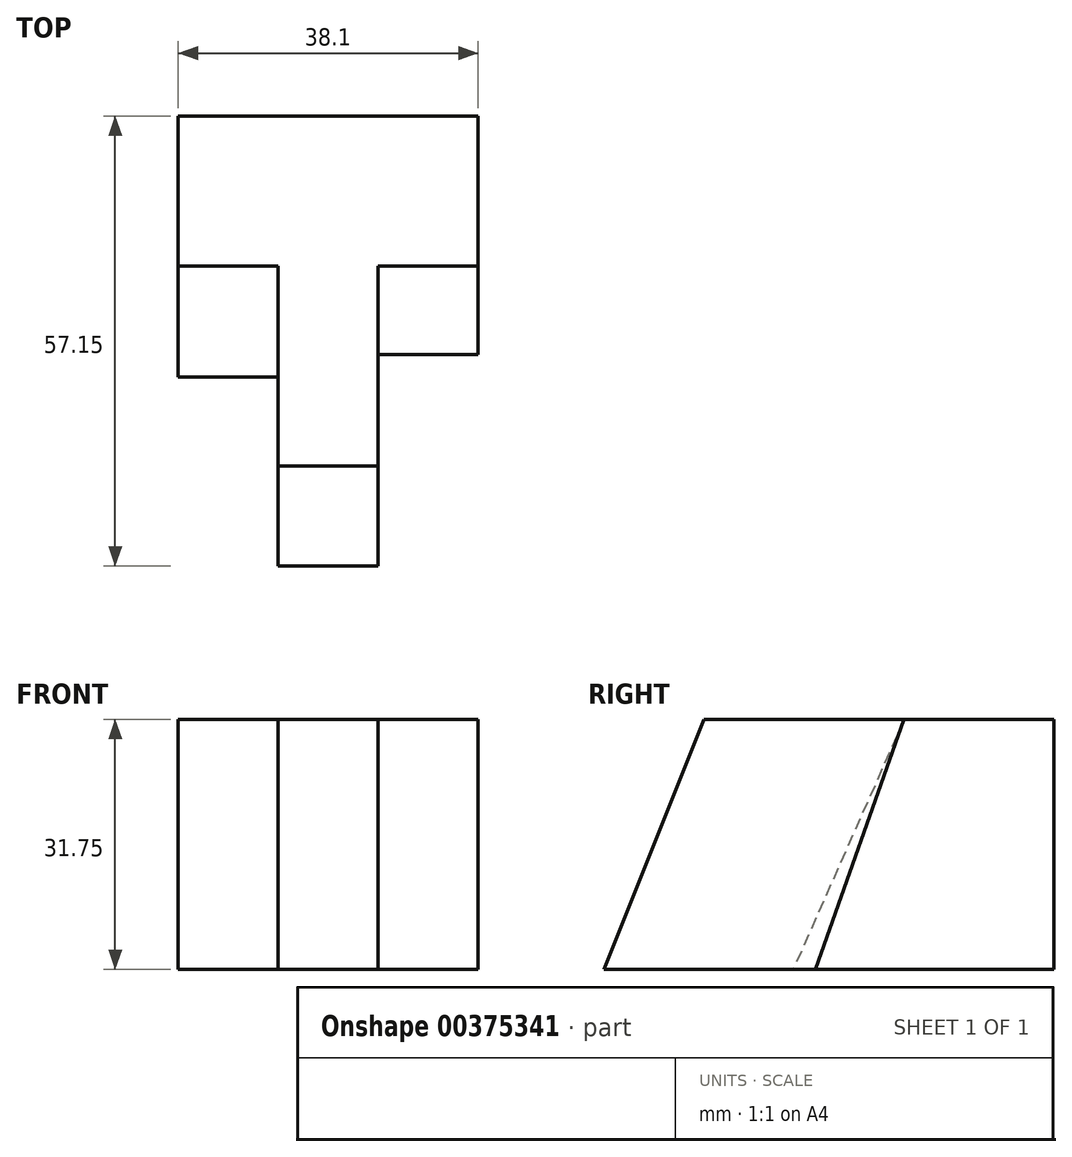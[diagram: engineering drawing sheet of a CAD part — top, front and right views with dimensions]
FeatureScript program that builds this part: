
annotation { "Feature Type Name" : "Feature", "Feature Type Description" : "" }
export const myFeature = defineFeature(function(context is Context, id is Id, definition is map)
    precondition{}
    {
        {
            var Q0;
            Q0=qCreatedBy(makeId("Top.planeOp"),FACE);
            var sketch = newSketch(context, id + "F0", { "sketchPlane" : qUnion([Q0])});
            skLineSegment(sketch, "E0", {"start": v(0, 0) * mm, "end": v(0, 25.4) * mm});
            skLineSegment(sketch, "E1", {"start": v(0, 25.4) * mm, "end": v(12.7, 25.4) * mm});
            skLineSegment(sketch, "E2", {"start": v(12.7, 25.4) * mm, "end": v(12.7, 44.45) * mm});
            skLineSegment(sketch, "E3", {"start": v(12.7, 44.45) * mm, "end": v(-25.4, 44.45) * mm});
            skLineSegment(sketch, "E4", {"start": v(-25.4, 44.45) * mm, "end": v(-25.4, 25.4) * mm});
            skLineSegment(sketch, "E5", {"start": v(-25.4, 25.4) * mm, "end": v(-12.7, 25.4) * mm});
            skLineSegment(sketch, "E6", {"start": v(-12.7, 25.4) * mm, "end": v(-12.7, 0) * mm});
            skLineSegment(sketch, "E7", {"start": v(-12.7, 0) * mm, "end": v(0, 0) * mm});
            skSolve(sketch);
        }
        {
            var Q0;
            Q0 = qSketchRegion(id + "F0", true);
            extrude(context, id + "F1", {"entities" : qUnion([Q0]), "depth" : 31.75 * mm});
        }
        {
            var Q0;
            Q0=makeQuery(id+"F1.opExtrude","SWEPT_FACE",FACE,{"disambiguationData":[OSD([sQuery(id+"F0.wireOp",EDGE,"E0")])]});
            var sketch = newSketch(context, id + "F2", { "sketchPlane" : qUnion([Q0])});
            skLineSegment(sketch, "E8", {"start": v(0, 0) * mm, "end": v(14.13, 0) * mm});
            skLineSegment(sketch, "E9", {"start": v(25.4, 31.75) * mm, "end": v(14.13, 0) * mm});
            skSolve(sketch);
        }
        {
            var Q0;
            Q0 = qSketchRegion(id + "F2", true);
            var Q1;
            {var subQ0=sQuery(id+"F2.wireOp",EDGE,"E9");Q1=makeQuery(id+"F2.imprint","IMPRINT",FACE,{"disambiguationData":[TD([[makeQuery(id+"F2.imprint","IMPRINT",EDGE,{"derivedFrom":subQ0}),1.0]])]});}
            extrude(context, id + "F3", {"entities" : qUnion([Q0, Q1]), "operationType" : NewBodyOperationType.ADD, "depth" : 12.7 * mm});
        }
        {
            var Q0;
            Q0=makeQuery(id+"F1.opExtrude","SWEPT_FACE",FACE,{"disambiguationData":[OSD([sQuery(id+"F0.wireOp",EDGE,"E6")])]});
            var sketch = newSketch(context, id + "F4", { "sketchPlane" : qUnion([Q0])});
            skLineSegment(sketch, "E10", {"start": v(0, 0) * mm, "end": v(-25.4, 0) * mm});
            skLineSegment(sketch, "E11", {"start": v(-25.4, 31.75) * mm, "end": v(-9.96, -3.08) * mm});
            skSolve(sketch);
        }
        {
            var Q0;
            Q0 = qSketchRegion(id + "F4", true);
            var Q1;
            {var subQ1=sQuery(id+"F0.wireOp",EDGE,"E6");var subQ2=makeQuery(id+"F1.opExtrude","SWEPT_EDGE",EDGE,{"disambiguationData":[OSD([sQuery(id+"F0.wireOp",EDGE,"E5"),subQ1])]});Q1=makeQuery(id+"F4.imprint","IMPRINT",FACE,{"disambiguationData":[TD([[makeQuery(id+"F4.imprint","IMPRINT",EDGE,{"derivedFrom":subQ2}),1.0]])]});}
            extrude(context, id + "F5", {"entities" : qUnion([Q0, Q1]), "operationType" : NewBodyOperationType.ADD, "depth" : 12.7 * mm});
        }
        {
            var Q0;
            Q0=makeQuery(id+"F1.opExtrude","SWEPT_FACE",FACE,{"disambiguationData":[OSD([sQuery(id+"F0.wireOp",EDGE,"E0")])]});
            var sketch = newSketch(context, id + "F6", { "sketchPlane" : qUnion([Q0])});
            skLineSegment(sketch, "E12", {"start": v(0, 0) * mm, "end": v(-12.7, 0) * mm});
            skLineSegment(sketch, "E13", {"start": v(-12.7, 0) * mm, "end": v(0, 31.75) * mm});
            skSolve(sketch);
        }
        {
            var Q0;
            Q0 = qSketchRegion(id + "F6", true);
            var Q1;
            {var subQ0=sQuery(id+"F0.wireOp",EDGE,"E0");Q1=makeQuery(id+"F6.imprint","IMPRINT",FACE,{"disambiguationData":[TD([[makeQuery(id+"F6.imprint","IMPRINT",EDGE,{"derivedFrom":makeQuery(id+"F1.opExtrude","CAP_EDGE",EDGE,{"disambiguationData":[OSD([subQ0])],"isStart":false})}),-1.0]])]});}
            var Q2;
            Q2=makeQuery(id+"F6.imprint","IMPRINT",FACE,{"disambiguationData":[TD([[makeQuery(id+"F6.imprint","IMPRINT",EDGE,{"derivedFrom":sQuery(id+"F6.wireOp",EDGE,"E12")}),-1.0]])]});
            extrude(context, id + "F7", {"entities" : qUnion([Q0, Q1, Q2]), "operationType" : NewBodyOperationType.ADD, "oppositeDirection" : true, "depth" : 12.7 * mm});
        }
    });
